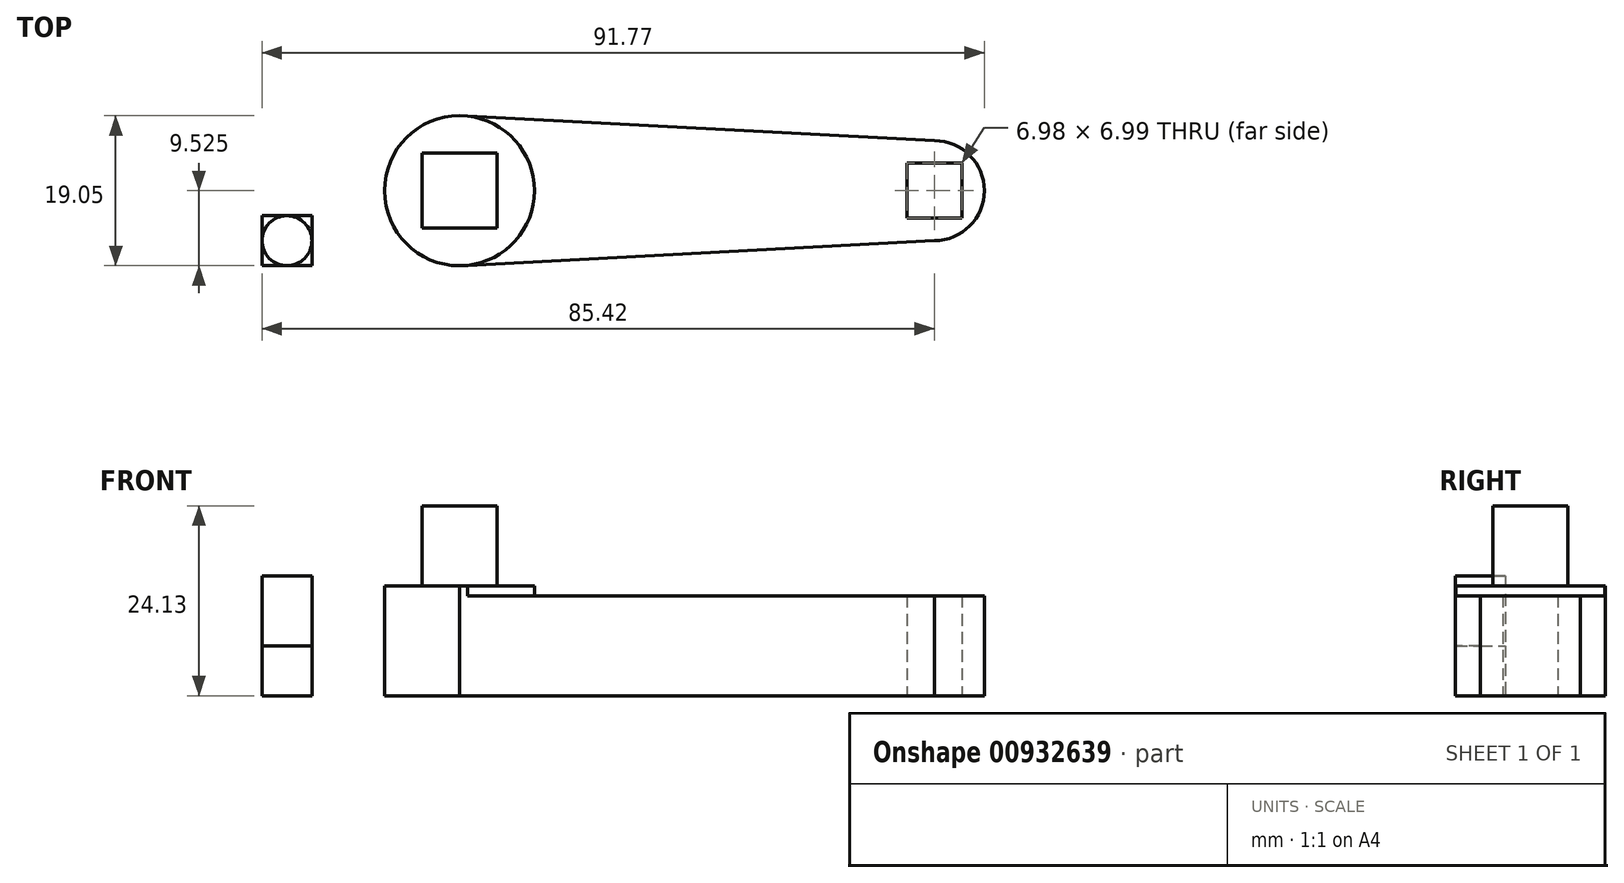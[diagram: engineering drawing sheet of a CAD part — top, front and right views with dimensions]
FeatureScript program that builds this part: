
annotation { "Feature Type Name" : "Feature", "Feature Type Description" : "" }
export const myFeature = defineFeature(function(context is Context, id is Id, definition is map)
    precondition{}
    {
        {
            var Q0;
            Q0=qCreatedBy(makeId("Top.planeOp"),FACE);
            var sketch = newSketch(context, id + "F0", { "sketchPlane" : qUnion([Q0])});
            skLineSegment(sketch, "E0", {"start": v(9.52, 9.53) * mm, "end": v(9.52, 0) * mm});
            skArc(sketch, "E1", {"start": v(9.53, 19.05) * mm, "mid": v(0, 9.53) * mm, "end": v(9.52, 0) * mm});
            skPoint(sketch, "E2.orphan", {"position": v(0, 0) * mm});
            skPoint(sketch, "E3.left.end.orphan", {"position": v(0, 19.05) * mm});
            skPoint(sketch, "E4.start.orphan", {"position": v(0, 9.53) * mm});
            skLineSegment(sketch, "E5", {"start": v(76.2, 9.53) * mm, "end": v(76.2, 0) * mm});
            skLineSegment(sketch, "E6", {"start": v(76.2, 9.53) * mm, "end": v(69.85, 9.53) * mm});
            skLineSegment(sketch, "E7", {"start": v(69.85, 9.53) * mm, "end": v(69.85, 15.88) * mm});
            skLineSegment(sketch, "E8", {"start": v(69.85, 9.53) * mm, "end": v(69.85, 3.17) * mm});
            skLineSegment(sketch, "E9", {"start": v(69.85, 3.17) * mm, "end": v(9.53, 0) * mm});
            skLineSegment(sketch, "E10", {"start": v(9.53, 19.05) * mm, "end": v(69.85, 15.88) * mm});
            skArc(sketch, "E11", {"start": v(69.85, 3.18) * mm, "mid": v(76.2, 9.53) * mm, "end": v(69.85, 15.88) * mm});
            skCircle(sketch, "E12", {"center": v(9.52, 9.53) * mm, "radius": 9.53 * mm});
            skLineSegment(sketch, "E13.trimOffspring", {"start": v(69.85, 9.53) * mm, "end": v(76.2, 9.53) * mm});
            skSolve(sketch);
        }
        {
            var Q0;
            {var subQ2=sQuery(id+"F0.wireOp",EDGE,"E1");Q0=makeQuery(id+"F0.imprint","IMPRINT",FACE,{"disambiguationData":[TD([[makeQuery(id+"F0.imprint","IMPRINT",EDGE,{"derivedFrom":subQ2}),1.0]])]});}
            extrude(context, id + "F1", {"entities" : qUnion([Q0]), "depth" : 13.97 * mm, "offsetDistance" : 25.4 * mm});
        }
        {
            var Q0;
            {var subQ2=sQuery(id+"F0.wireOp",EDGE,"E7");Q0=makeQuery(id+"F0.imprint","IMPRINT",FACE,{"disambiguationData":[TD([[makeQuery(id+"F0.imprint","IMPRINT",EDGE,{"derivedFrom":subQ2}),1.0]])]});}
            var Q1;
            {var subQ0=sQuery(id+"F0.wireOp",EDGE,"E6");Q1=makeQuery(id+"F0.imprint","IMPRINT",FACE,{"disambiguationData":[TD([[makeQuery(id+"F0.imprint","IMPRINT",EDGE,{"derivedFrom":subQ0}),-1.0]])]});}
            var Q2;
            {var subQ0=sQuery(id+"F0.wireOp",EDGE,"E6");Q2=makeQuery(id+"F0.imprint","IMPRINT",FACE,{"disambiguationData":[TD([[makeQuery(id+"F0.imprint","IMPRINT",EDGE,{"derivedFrom":subQ0}),1.0]])]});}
            extrude(context, id + "F2", {"entities" : qUnion([Q0, Q1, Q2]), "operationType" : NewBodyOperationType.ADD, "depth" : 12.7 * mm, "offsetDistance" : 25.4 * mm});
        }
        {
            var Q0;
            Q0=makeQuery(id+"F1.opExtrude","CAP_FACE",FACE,{"disambiguationData":[OSD([sQuery(id+"F0.wireOp",EDGE,"E1"),sQuery(id+"F0.wireOp",EDGE,"E9"),sQuery(id+"F0.wireOp",EDGE,"E10"),sQuery(id+"F0.wireOp",EDGE,"E12")])],"isStart":false});
            var sketch = newSketch(context, id + "F3", { "sketchPlane" : qUnion([Q0])});
            skLineSegment(sketch, "E14.bottom", {"start": v(14.29, 4.76) * mm, "end": v(4.76, 4.76) * mm});
            skLineSegment(sketch, "E14.top", {"start": v(14.29, 14.29) * mm, "end": v(4.76, 14.29) * mm});
            skLineSegment(sketch, "E14.left", {"start": v(14.29, 4.76) * mm, "end": v(14.29, 14.29) * mm});
            skLineSegment(sketch, "E14.right", {"start": v(4.76, 4.76) * mm, "end": v(4.76, 14.29) * mm});
            skPoint(sketch, "E14.middle", {"position": v(9.52, 9.53) * mm});
            skSolve(sketch);
        }
        {
            var Q0;
            Q0=makeQuery(id+"F3.imprint","IMPRINT",FACE,{"disambiguationData":[TD([[makeQuery(id+"F3.imprint","IMPRINT",EDGE,{"derivedFrom":sQuery(id+"F3.wireOp",EDGE,"E14.bottom")}),-1.0]])]});
            extrude(context, id + "F4", {"entities" : qUnion([Q0]), "operationType" : NewBodyOperationType.ADD, "depth" : 10.16 * mm, "offsetDistance" : 25.4 * mm});
        }
        {
            var Q0;
            Q0=qCreatedBy(makeId("Top.planeOp"),FACE);
            var sketch = newSketch(context, id + "F5", { "sketchPlane" : qUnion([Q0])});
            skLineSegment(sketch, "E15", {"start": v(0, 0) * mm, "end": v(0, 9.53) * mm});
            skLineSegment(sketch, "E16", {"start": v(0, 9.53) * mm, "end": v(69.85, 9.53) * mm});
            skLineSegment(sketch, "E17.bottom", {"start": v(73.34, 6.03) * mm, "end": v(66.36, 6.03) * mm});
            skLineSegment(sketch, "E17.top", {"start": v(73.34, 13.02) * mm, "end": v(66.36, 13.02) * mm});
            skLineSegment(sketch, "E17.left", {"start": v(73.34, 6.03) * mm, "end": v(73.34, 13.02) * mm});
            skLineSegment(sketch, "E17.right", {"start": v(66.36, 6.03) * mm, "end": v(66.36, 13.02) * mm});
            skPoint(sketch, "E17.middle", {"position": v(69.85, 9.53) * mm});
            skSolve(sketch);
        }
        {
            var Q0;
            {var subQ3=sQuery(id+"F5.wireOp",EDGE,"E17.bottom");Q0=makeQuery(id+"F5.imprint","IMPRINT",FACE,{"disambiguationData":[TD([[makeQuery(id+"F5.imprint","IMPRINT",EDGE,{"derivedFrom":subQ3}),-1.0]])]});}
            extrude(context, id + "F6", {"entities" : qUnion([Q0]), "operationType" : NewBodyOperationType.REMOVE, "endBound" : BoundingType.THROUGH_ALL, "depth" : 25.4 * mm, "offsetDistance" : 25.4 * mm});
        }
        {
            var Q0;
            Q0=qCreatedBy(makeId("Top.planeOp"),FACE);
            var sketch = newSketch(context, id + "F7", { "sketchPlane" : qUnion([Q0])});
            skLineSegment(sketch, "E18.bottom", {"start": v(-9.22, 0) * mm, "end": v(-15.57, 0) * mm});
            skLineSegment(sketch, "E18.top", {"start": v(-9.22, 6.35) * mm, "end": v(-15.57, 6.35) * mm});
            skLineSegment(sketch, "E18.left", {"start": v(-9.22, 0) * mm, "end": v(-9.22, 6.35) * mm});
            skLineSegment(sketch, "E18.right", {"start": v(-15.57, 0) * mm, "end": v(-15.57, 6.35) * mm});
            skSolve(sketch);
        }
        {
            var Q0;
            Q0=makeQuery(id+"F7.imprint","IMPRINT",FACE,{"disambiguationData":[TD([[makeQuery(id+"F7.imprint","IMPRINT",EDGE,{"derivedFrom":sQuery(id+"F7.wireOp",EDGE,"E18.bottom")}),-1.0]])]});
            extrude(context, id + "F8", {"entities" : qUnion([Q0]), "depth" : 6.35 * mm, "offsetDistance" : 25.4 * mm});
        }
        {
            var Q0;
            Q0=makeQuery(id+"F8.opExtrude","CAP_FACE",FACE,{"disambiguationData":[OSD([sQuery(id+"F7.wireOp",EDGE,"E18.bottom"),sQuery(id+"F7.wireOp",EDGE,"E18.top"),sQuery(id+"F7.wireOp",EDGE,"E18.left"),sQuery(id+"F7.wireOp",EDGE,"E18.right")])],"isStart":false});
            var sketch = newSketch(context, id + "F9", { "sketchPlane" : qUnion([Q0])});
            skLineSegment(sketch, "E19", {"start": v(-15.57, 6.35) * mm, "end": v(-14.64, 5.42) * mm});
            skLineSegment(sketch, "E20", {"start": v(-9.22, 0) * mm, "end": v(-9.22, 6.35) * mm});
            skLineSegment(sketch, "E21", {"start": v(-15.57, 0) * mm, "end": v(-14.64, 0.93) * mm});
            skCircle(sketch, "E22", {"center": v(-12.4, 3.18) * mm, "radius": 3.18 * mm});
            skLineSegment(sketch, "E23.trimOffspring", {"start": v(-10.15, 0.93) * mm, "end": v(-9.22, 0) * mm});
            skLineSegment(sketch, "E24.trimOffspring", {"start": v(-10.15, 5.42) * mm, "end": v(-9.22, 6.35) * mm});
            skPoint(sketch, "E25.start.orphan", {"position": v(-9.22, 3.18) * mm});
            skPoint(sketch, "E26.end.orphan", {"position": v(-12.4, 6.35) * mm});
            skSolve(sketch);
        }
        {
            var Q0;
            {var subQ0=sQuery(id+"F9.wireOp",EDGE,"E22");var subQ4=makeQuery(id+"F9.imprint","INTERSECT",VERTEX,{"derivedFrom":[subQ0,sQuery(id+"F9.wireOp",EDGE,"E24.trimOffspring")]});Q0=makeQuery(id+"F9.imprint","IMPRINT",FACE,{"disambiguationData":[TD([[makeQuery(id+"F9.imprint","IMPRINT",EDGE,{"disambiguationData":[TD([[subQ4,1.0]])],"derivedFrom":subQ0}),1.0]])]});}
            var sketch = newSketch(context, id + "F10", { "sketchPlane" : qUnion([Q0])});
            skSolve(sketch);
        }
        {
            var Q0;
            {var subQ0=sQuery(id+"F9.wireOp",EDGE,"E22");var subQ4=makeQuery(id+"F9.imprint","INTERSECT",VERTEX,{"derivedFrom":[subQ0,sQuery(id+"F9.wireOp",EDGE,"E24.trimOffspring")]});Q0=makeQuery(id+"F10.imprint","IMPRINT",FACE,{"disambiguationData":[TD([[makeQuery(id+"F10.imprint","IMPRINT",EDGE,{"derivedFrom":makeQuery(id+"F9.imprint","IMPRINT",EDGE,{"disambiguationData":[TD([[subQ4,1.0]])],"derivedFrom":subQ0})}),1.0]])]});}
            extrude(context, id + "F11", {"entities" : qUnion([Q0]), "operationType" : NewBodyOperationType.ADD, "depth" : 8.9 * mm, "offsetDistance" : 25.4 * mm});
        }
    });
